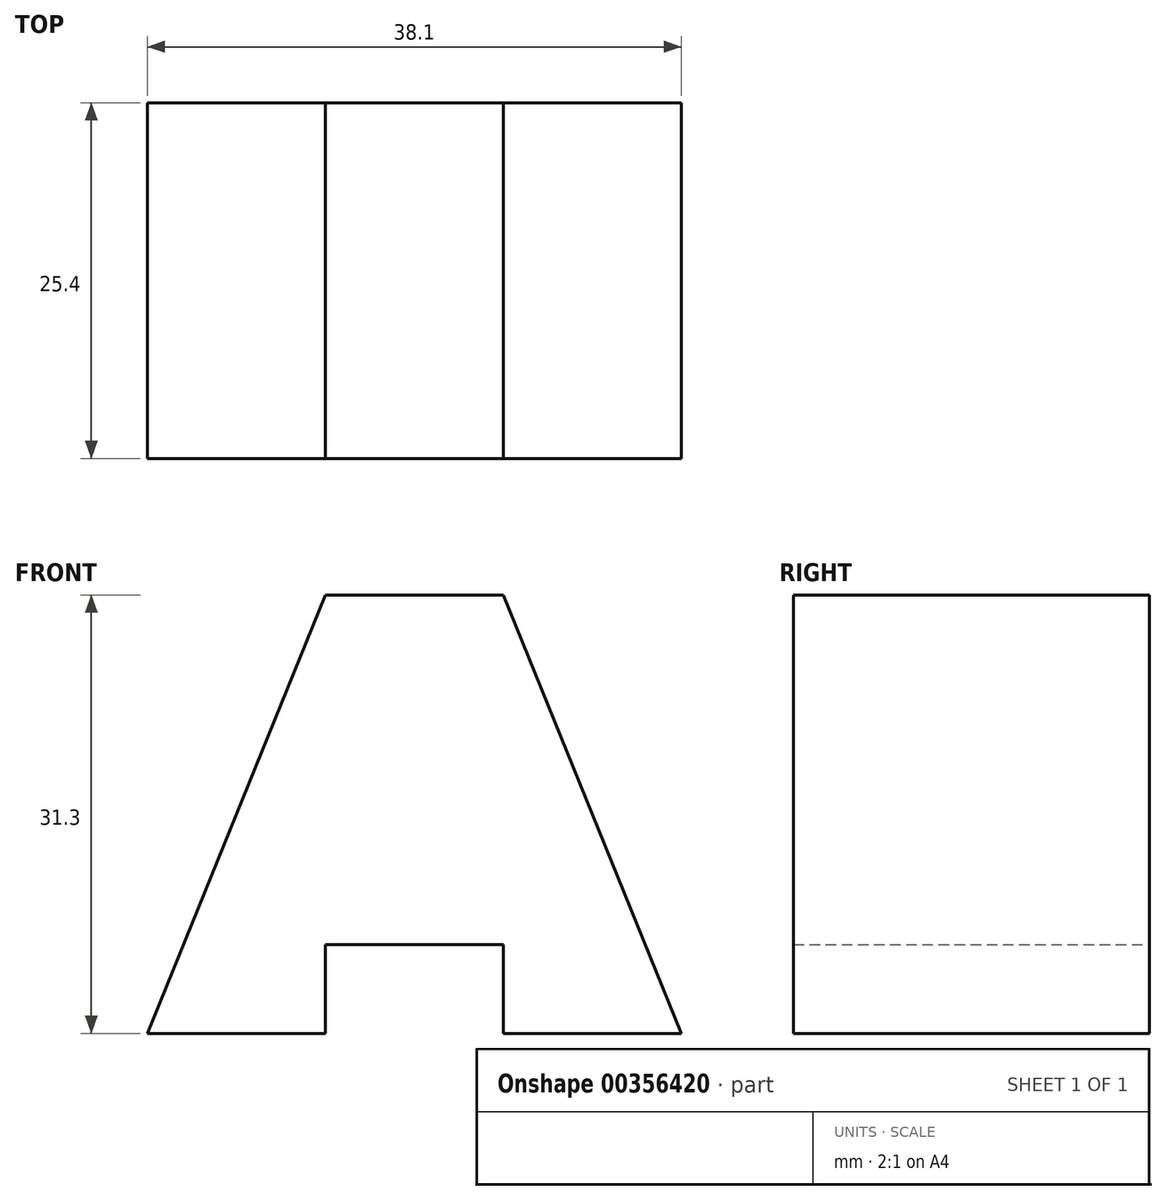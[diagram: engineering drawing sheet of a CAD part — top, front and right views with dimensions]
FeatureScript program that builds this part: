
annotation { "Feature Type Name" : "Feature", "Feature Type Description" : "" }
export const myFeature = defineFeature(function(context is Context, id is Id, definition is map)
    precondition{}
    {
        {
            var Q0;
            Q0=qCreatedBy(makeId("Front.planeOp"),FACE);
            var sketch = newSketch(context, id + "F0", { "sketchPlane" : qUnion([Q0])});
            skLineSegment(sketch, "E0", {"start": v(0, 0) * mm, "end": v(12.7, 0) * mm});
            skLineSegment(sketch, "E1", {"start": v(12.7, 0) * mm, "end": v(12.7, 6.35) * mm});
            skLineSegment(sketch, "E2", {"start": v(12.7, 6.35) * mm, "end": v(25.4, 6.35) * mm});
            skLineSegment(sketch, "E3", {"start": v(25.4, 6.35) * mm, "end": v(25.4, 0) * mm});
            skLineSegment(sketch, "E4", {"start": v(25.4, 0) * mm, "end": v(38.1, 0) * mm});
            skLineSegment(sketch, "E5", {"start": v(38.1, 0) * mm, "end": v(25.4, 31.3) * mm});
            skLineSegment(sketch, "E6", {"start": v(25.4, 31.3) * mm, "end": v(12.7, 31.3) * mm});
            skLineSegment(sketch, "E7", {"start": v(12.7, 31.3) * mm, "end": v(0, 0) * mm});
            skSolve(sketch);
        }
        {
            var Q0;
            Q0 = qSketchRegion(id + "F0", true);
            extrude(context, id + "F1", {"entities" : qUnion([Q0]), "depth" : 25.4 * mm});
        }
    });
